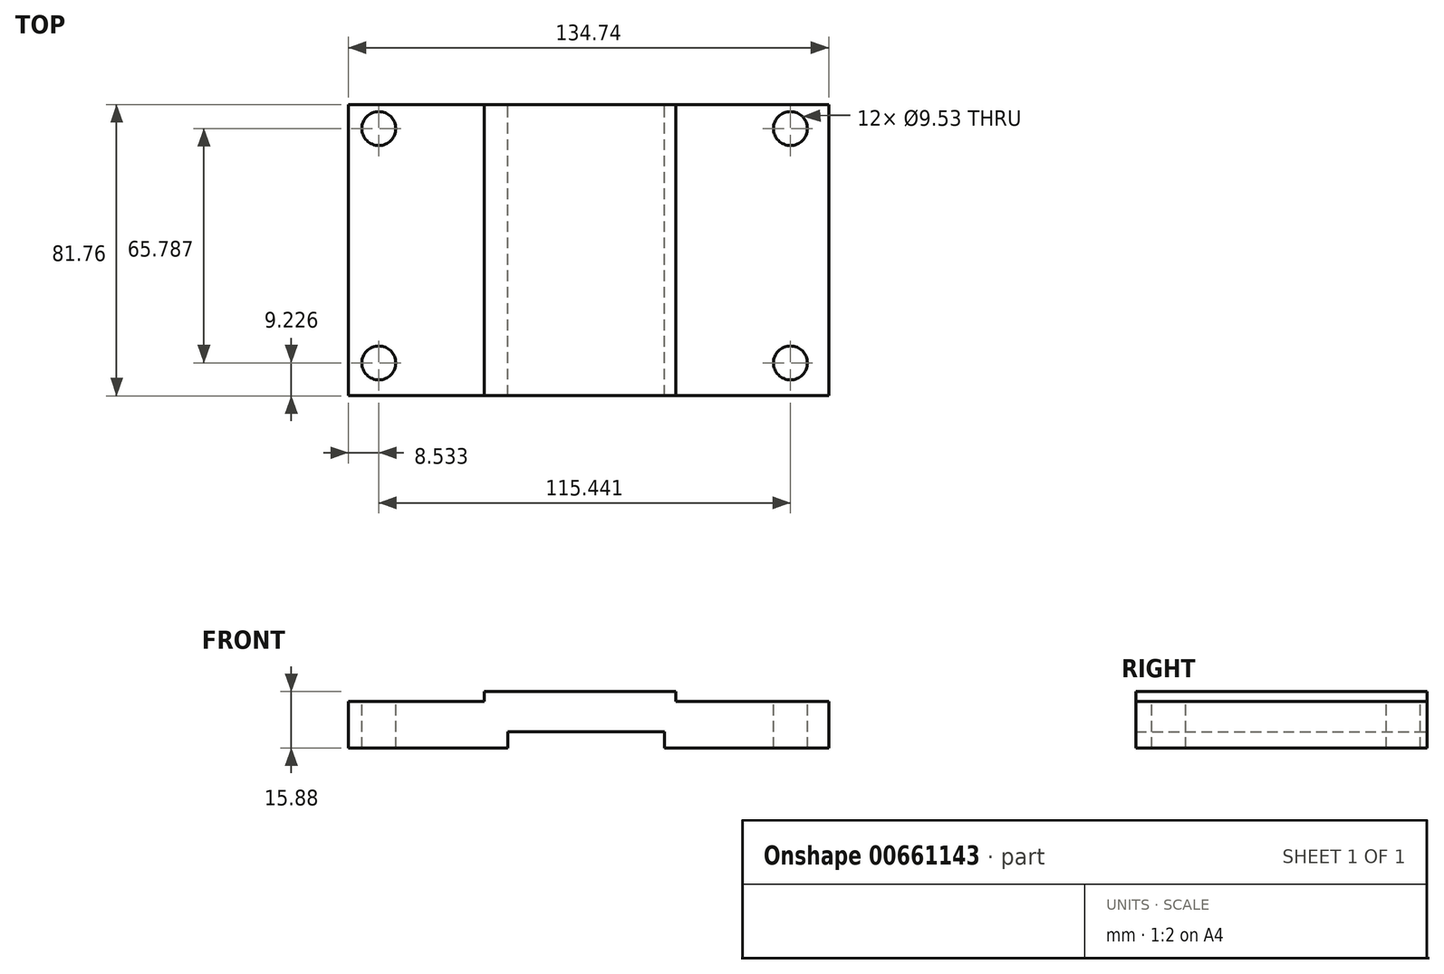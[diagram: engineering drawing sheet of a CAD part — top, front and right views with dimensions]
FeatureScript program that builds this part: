
annotation { "Feature Type Name" : "Feature", "Feature Type Description" : "" }
export const myFeature = defineFeature(function(context is Context, id is Id, definition is map)
    precondition{}
    {
        {
            var Q0;
            Q0=qCreatedBy(makeId("Front.planeOp"),FACE);
            var sketch = newSketch(context, id + "F0", { "sketchPlane" : qUnion([Q0])});
            skLineSegment(sketch, "E0", {"start": v(0, 0) * mm, "end": v(0, 13.1) * mm});
            skLineSegment(sketch, "E1", {"start": v(0, 13.1) * mm, "end": v(38.1, 13.1) * mm});
            skLineSegment(sketch, "E2", {"start": v(38.1, 13.1) * mm, "end": v(38.1, 15.88) * mm});
            skLineSegment(sketch, "E3", {"start": v(38.1, 15.88) * mm, "end": v(91.88, 15.88) * mm});
            skLineSegment(sketch, "E4", {"start": v(91.88, 15.88) * mm, "end": v(91.88, 13.1) * mm});
            skLineSegment(sketch, "E5", {"start": v(0, 0) * mm, "end": v(44.65, 0) * mm});
            skLineSegment(sketch, "E6", {"start": v(44.65, 0) * mm, "end": v(44.65, 4.54) * mm});
            skLineSegment(sketch, "E7", {"start": v(44.65, 4.54) * mm, "end": v(88.7, 4.54) * mm});
            skLineSegment(sketch, "E8", {"start": v(88.7, 4.54) * mm, "end": v(88.7, 0) * mm});
            skLineSegment(sketch, "E9", {"start": v(88.7, 0) * mm, "end": v(134.74, 0) * mm});
            skLineSegment(sketch, "E10", {"start": v(134.74, 0) * mm, "end": v(134.74, 13.1) * mm});
            skLineSegment(sketch, "E11", {"start": v(134.74, 13.1) * mm, "end": v(91.88, 13.1) * mm});
            skSolve(sketch);
        }
        {
            var Q0;
            Q0=makeQuery(id+"F0.imprint","IMPRINT",FACE,{"disambiguationData":[TD([[makeQuery(id+"F0.imprint","IMPRINT",EDGE,{"derivedFrom":sQuery(id+"F0.wireOp",EDGE,"E0")}),-1.0]])]});
            extrude(context, id + "F1", {"entities" : qUnion([Q0]), "depth" : 81.76 * mm, "offsetDistance" : 25.4 * mm});
        }
        {
            var Q0;
            Q0=makeQuery(id+"F1.opExtrude","SWEPT_FACE",FACE,{"disambiguationData":[OSD([sQuery(id+"F0.wireOp",EDGE,"E1")])]});
            var sketch = newSketch(context, id + "F2", { "sketchPlane" : qUnion([Q0])});
            skLineSegment(sketch, "E12.bottom", {"start": v(0, 0) * mm, "end": v(8.53, 0) * mm});
            skLineSegment(sketch, "E12.left", {"start": v(0, 0) * mm, "end": v(0, -6.75) * mm});
            skCircle(sketch, "E13", {"center": v(8.53, -6.75) * mm, "radius": 4.76 * mm});
            skCircle(sketch, "E14", {"center": v(8.53, -72.53) * mm, "radius": 4.76 * mm});
            skCircle(sketch, "E15", {"center": v(123.97, -6.75) * mm, "radius": 4.76 * mm});
            skCircle(sketch, "E16", {"center": v(123.97, -72.53) * mm, "radius": 4.76 * mm});
            skSolve(sketch);
        }
        {
            var Q0;
            Q0 = qSketchRegion(id + "F2", true);
            extrude(context, id + "F3", {"entities" : qUnion([Q0]), "operationType" : NewBodyOperationType.REMOVE, "oppositeDirection" : true, "depth" : 25.4 * mm, "offsetDistance" : 25.4 * mm});
        }
    });
